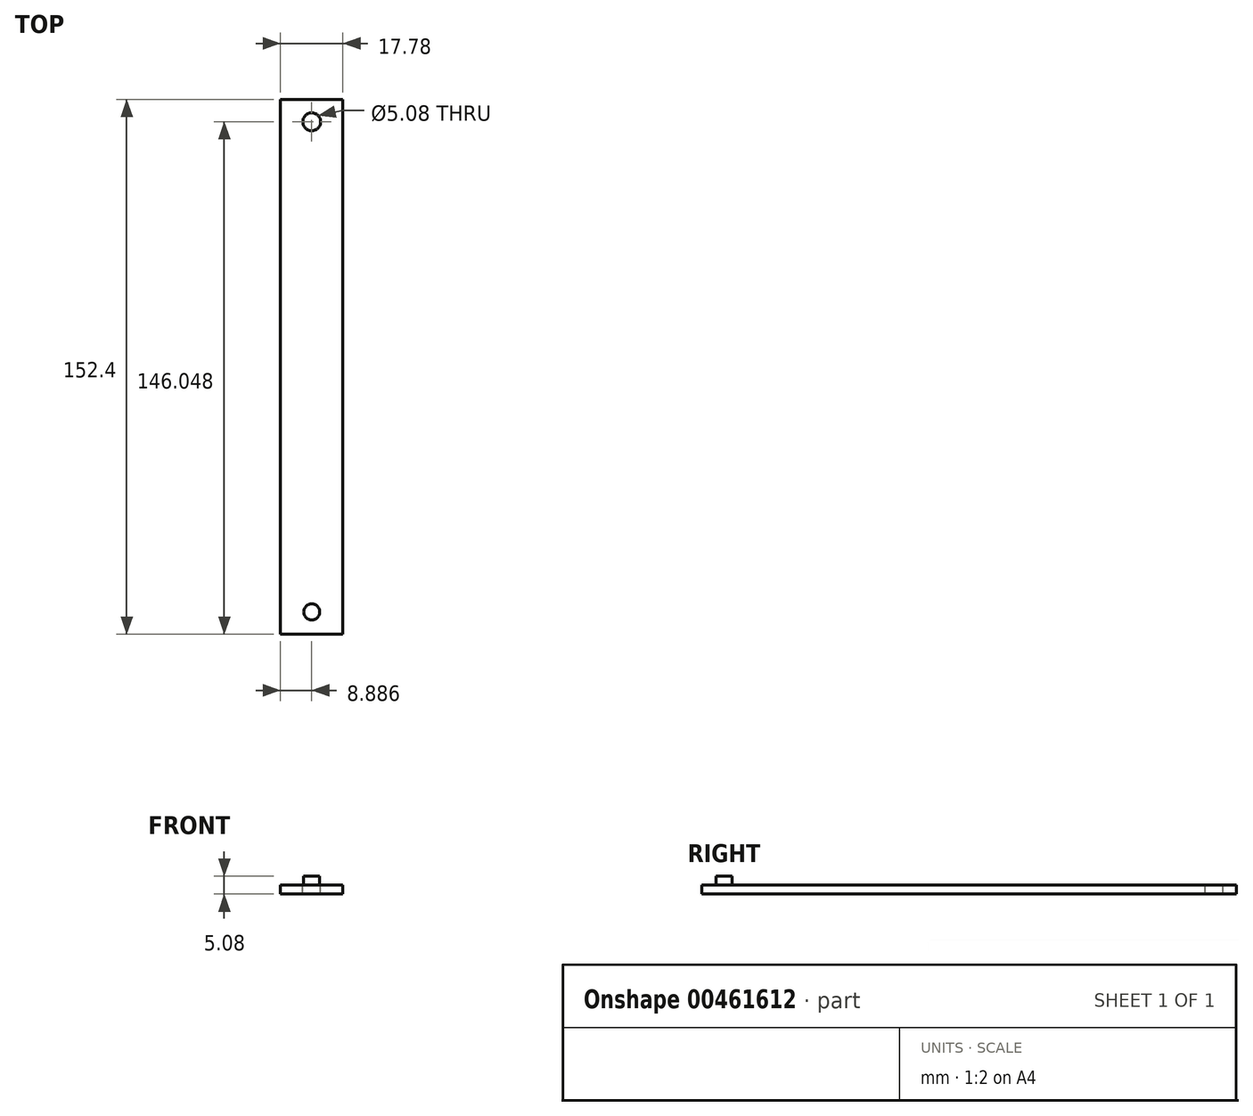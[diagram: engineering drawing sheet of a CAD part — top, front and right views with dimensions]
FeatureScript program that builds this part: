
annotation { "Feature Type Name" : "Feature", "Feature Type Description" : "" }
export const myFeature = defineFeature(function(context is Context, id is Id, definition is map)
    precondition{}
    {
        {
            var Q0;
            Q0=qCreatedBy(makeId("Top.planeOp"),FACE);
            var sketch = newSketch(context, id + "F0", { "sketchPlane" : qUnion([Q0])});
            skLineSegment(sketch, "E0.bottom", {"start": v(-16.93, -8.82) * mm, "end": v(0.85, -8.82) * mm});
            skLineSegment(sketch, "E0.top", {"start": v(-16.93, 143.58) * mm, "end": v(0.85, 143.58) * mm});
            skLineSegment(sketch, "E0.left", {"start": v(-16.93, -8.82) * mm, "end": v(-16.93, 143.58) * mm});
            skLineSegment(sketch, "E0.right", {"start": v(0.85, -8.82) * mm, "end": v(0.85, 143.58) * mm});
            skSolve(sketch);
        }
        {
            var Q0;
            Q0 = qSketchRegion(id + "F0", true);
            extrude(context, id + "F1", {"entities" : qUnion([Q0]), "depth" : 2.54 * mm});
        }
        {
            var Q0;
            Q0=makeQuery(id+"F1.opExtrude","CAP_FACE",FACE,{"disambiguationData":[OSD([sQuery(id+"F0.wireOp",EDGE,"E0.bottom"),sQuery(id+"F0.wireOp",EDGE,"E0.top"),sQuery(id+"F0.wireOp",EDGE,"E0.left"),sQuery(id+"F0.wireOp",EDGE,"E0.right")])],"isStart":false});
            var sketch = newSketch(context, id + "F2", { "sketchPlane" : qUnion([Q0])});
            skLineSegment(sketch, "E1", {"start": v(-8.04, 143.58) * mm, "end": v(-8.04, 137.23) * mm});
            skCircle(sketch, "E2", {"center": v(-8.04, 137.23) * mm, "radius": 2.54 * mm});
            skSolve(sketch);
        }
        {
            var Q0;
            Q0 = qSketchRegion(id + "F2", true);
            extrude(context, id + "F3", {"entities" : qUnion([Q0]), "operationType" : NewBodyOperationType.REMOVE, "endBound" : BoundingType.THROUGH_ALL, "oppositeDirection" : true, "depth" : 25.4 * mm});
        }
        {
            var Q0;
            Q0=makeQuery(id+"F1.opExtrude","CAP_FACE",FACE,{"disambiguationData":[OSD([sQuery(id+"F0.wireOp",EDGE,"E0.bottom"),sQuery(id+"F0.wireOp",EDGE,"E0.top"),sQuery(id+"F0.wireOp",EDGE,"E0.left"),sQuery(id+"F0.wireOp",EDGE,"E0.right")])],"isStart":false});
            var sketch = newSketch(context, id + "F4", { "sketchPlane" : qUnion([Q0])});
            skLineSegment(sketch, "E3", {"start": v(-8.04, -8.82) * mm, "end": v(-8.04, -2.47) * mm});
            skCircle(sketch, "E4", {"center": v(-8.04, -2.47) * mm, "radius": 2.29 * mm});
            skSolve(sketch);
        }
        {
            var Q0;
            Q0 = qSketchRegion(id + "F4", true);
            extrude(context, id + "F5", {"entities" : qUnion([Q0]), "operationType" : NewBodyOperationType.ADD, "depth" : 2.54 * mm});
        }
    });
